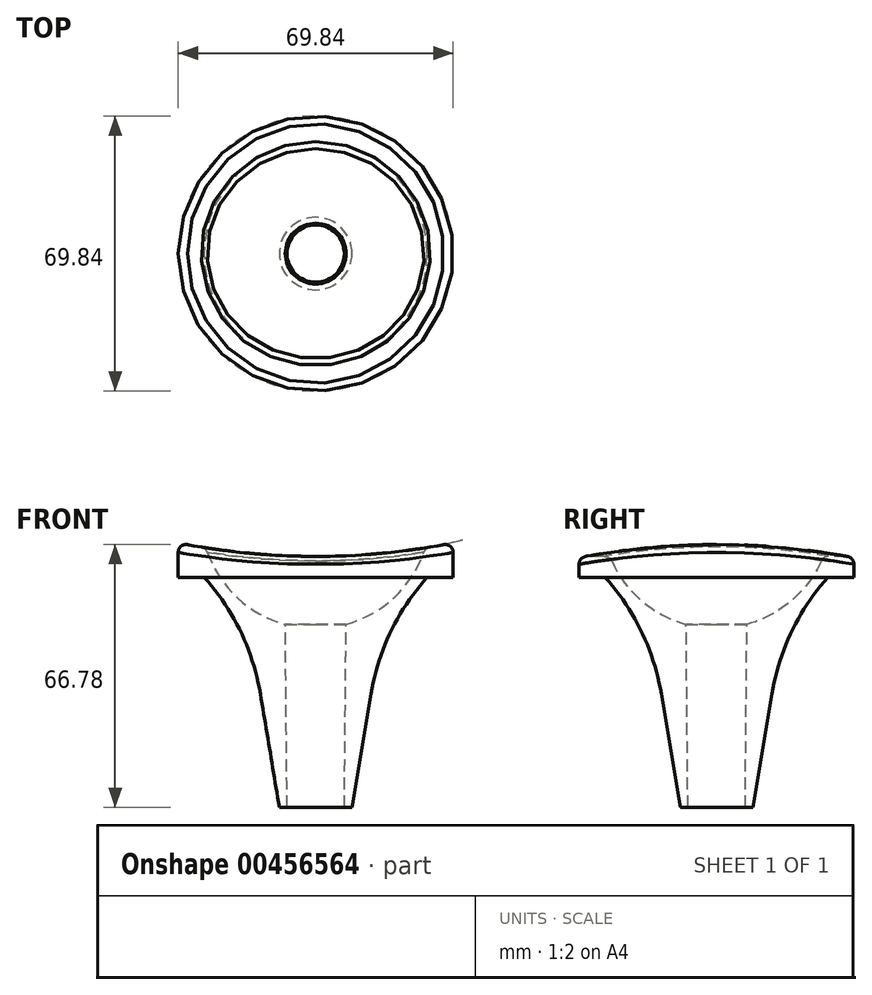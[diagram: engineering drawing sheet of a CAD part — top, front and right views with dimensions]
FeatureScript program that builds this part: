
annotation { "Feature Type Name" : "Feature", "Feature Type Description" : "" }
export const myFeature = defineFeature(function(context is Context, id is Id, definition is map)
    precondition{}
    {
        {
            var Q0;
            Q0=qCreatedBy(makeId("Front.planeOp"),FACE);
            var sketch = newSketch(context, id + "F0", { "sketchPlane" : qUnion([Q0])});
            skLineSegment(sketch, "E0", {"start": v(7.28, 0) * mm, "end": v(7.72, 46.5) * mm});
            skArc(sketch, "E1", {"start": v(7.72, 46.5) * mm, "mid": v(20.76, 54.1) * mm, "end": v(28.28, 67.2) * mm});
            skLineSegment(sketch, "E2", {"start": v(28.28, 67.2) * mm, "end": v(34.92, 67.2) * mm});
            skLineSegment(sketch, "E3", {"start": v(34.92, 67.2) * mm, "end": v(34.92, 58.47) * mm});
            skLineSegment(sketch, "E4", {"start": v(34.92, 58.47) * mm, "end": v(28.34, 58.47) * mm});
            skArc(sketch, "E5", {"start": v(28.34, 58.47) * mm, "mid": v(19.08, 44.66) * mm, "end": v(14.04, 28.8) * mm});
            skLineSegment(sketch, "E6", {"start": v(14.04, 28.8) * mm, "end": v(9.22, 0) * mm});
            skLineSegment(sketch, "E7", {"start": v(9.22, 0) * mm, "end": v(7.28, 0) * mm});
            skLineSegment(sketch, "E8", {"start": v(0, 0) * mm, "end": v(0, 58.4) * mm, "construction": true});
            skSolve(sketch);
        }
        {
            var Q0;
            Q0=makeQuery(id+"F0.imprint","IMPRINT",FACE,{"disambiguationData":[TD([[makeQuery(id+"F0.imprint","IMPRINT",EDGE,{"derivedFrom":sQuery(id+"F0.wireOp",EDGE,"E0")}),-1.0]])]});
            var Q1;
            Q1=sQuery(id+"F0.wireOp",EDGE,"E8");
            revolve(context, id + "F1", {"entities" : qUnion([Q0]), "axis" : qUnion([Q1]), "revolveType" : RevolveType.FULL});
        }
        {
            var Q0;
            Q0=qCreatedBy(makeId("Front.planeOp"),FACE);
            var sketch = newSketch(context, id + "F2", { "sketchPlane" : qUnion([Q0])});
            skArc(sketch, "E9", {"start": v(-34.92, 67.2) * mm, "mid": v(0, 63.77) * mm, "end": v(34.92, 67.2) * mm});
            skLineSegment(sketch, "E10.0", {"start": v(34.92, 67.2) * mm, "end": v(-34.92, 67.2) * mm});
            skSolve(sketch);
        }
        {
            var Q0;
            Q0 = qSketchRegion(id + "F2", true);
            extrude(context, id + "F3", {"entities" : qUnion([Q0]), "operationType" : NewBodyOperationType.REMOVE, "endBound" : BoundingType.THROUGH_ALL, "oppositeDirection" : true, "depth" : 25.4 * mm, "hasSecondDirection" : true, "secondDirectionBound" : SecondDirectionBoundingType.THROUGH_ALL, "secondDirectionOppositeDirection" : false, "secondDirectionDepth" : 25.4 * mm});
        }
        {
            var Q0;
            Q0=makeQuery(id+"F3.boolean.opBoolean","INTERSECT",EDGE,{"derivedFrom":[makeQuery(id+"F1.opRevolve","SWEPT_FACE",FACE,{"disambiguationData":[OSD([sQuery(id+"F0.wireOp",EDGE,"E1")])]}),makeQuery(id+"F3.opExtrude","SWEPT_FACE",FACE,{"disambiguationData":[OSD([sQuery(id+"F2.wireOp",EDGE,"E9")])]})]});
            var Q1;
            Q1=makeQuery(id+"F3.boolean.opBoolean","INTERSECT",EDGE,{"derivedFrom":[makeQuery(id+"F1.opRevolve","SWEPT_FACE",FACE,{"disambiguationData":[OSD([sQuery(id+"F0.wireOp",EDGE,"E3")])]}),makeQuery(id+"F3.opExtrude","SWEPT_FACE",FACE,{"disambiguationData":[OSD([sQuery(id+"F2.wireOp",EDGE,"E9")])]})]});
            fillet(context, id + "F4", {"entities" : qUnion([Q0, Q1]), "radius" : 2 * mm, "tangentPropagation" : true, "allowEdgeOverflow" : false});
        }
    });
